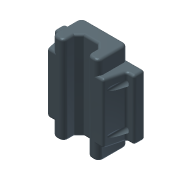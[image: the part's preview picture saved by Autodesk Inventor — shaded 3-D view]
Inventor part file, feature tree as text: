
AUTODESK INVENTOR PART (.ipt)
format: ipt  version: 2014 (Build 180170000, 170)  size: 267,776 bytes
history: native  units: mm
features: extrude x3, fillet x3, sketch x3, chamfer x1, mirror x1, plane x1
ambient origin geometry x8: Origin, YZ Plane, XZ Plane, XY Plane, X Axis, Y Axis, Z Axis, Center Point
bodies: Solid1 (feature_tree)
feature tree (12):
  extrude  "Extrusion1"  Depth=19.0mm
  chamfer  "Chamfer1"  Distance=56.9mm
  fillet  "Fillet1"  Radius=2.0mm
  fillet  "Fillet2"  Radius=3.0mm
  extrude  "Extrusion2"  Depth=2.0mm
  fillet  "Fillet3"  Radius=7.0mm
  mirror  "Mirror1"
  extrude  "Extrusion3"  Depth=2.0mm
  sketch  "Sketch1"  dims[d0=15.0mm d1=19.0mm]
  sketch  "Sketch2"  dims[d2=30.0mm]
  plane  "Work Plane1"
  sketch  "Sketch3"  dims[d3=10.0mm d4=56.9mm d5=0.0mm d6=3.0mm d7=2.0mm d8=45.0deg d9=3.0mm d10=1.5mm d11=7.0mm d12=26.0mm d13=6.0mm d14=5.0mm d15=38.7mm d16=0.0mm d17=1.5mm d18=26.0mm d19=41.0mm d20=4.0mm d21=5.0mm d22=0.0mm]
